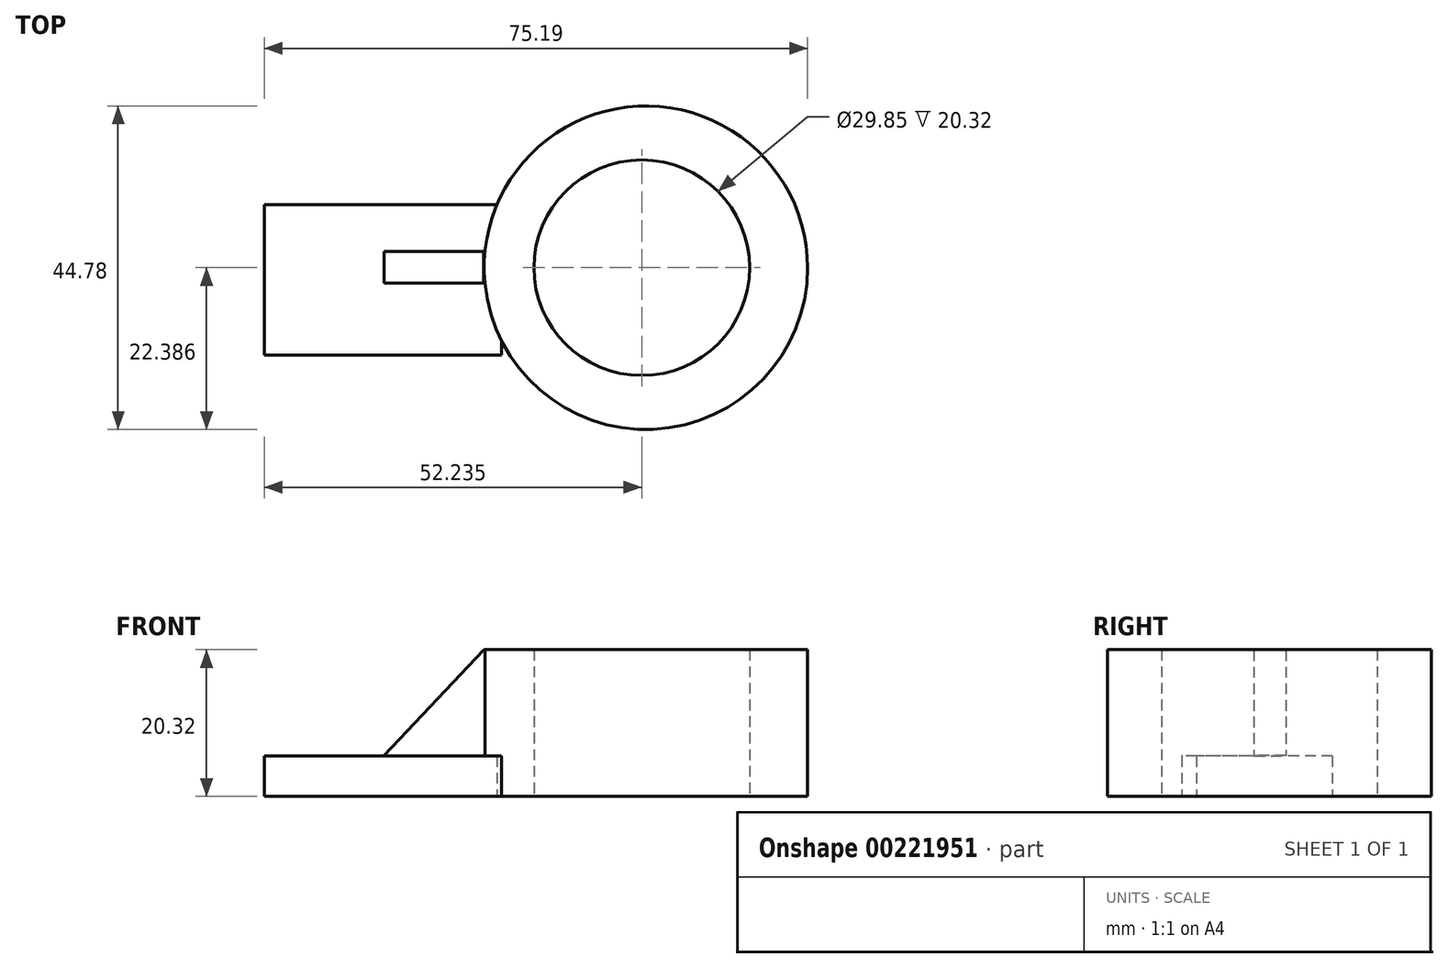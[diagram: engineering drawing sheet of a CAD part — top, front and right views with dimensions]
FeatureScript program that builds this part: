
annotation { "Feature Type Name" : "Feature", "Feature Type Description" : "" }
export const myFeature = defineFeature(function(context is Context, id is Id, definition is map)
    precondition{}
    {
        {
            var Q0;
            Q0=qCreatedBy(makeId("Top.planeOp"),FACE);
            var sketch = newSketch(context, id + "F0", { "sketchPlane" : qUnion([Q0])});
            skCircle(sketch, "E0", {"center": v(36.23, 28.1) * mm, "radius": 22.39 * mm});
            skSolve(sketch);
        }
        {
            var Q0;
            Q0 = qSketchRegion(id + "F0", true);
            extrude(context, id + "F1", {"entities" : qUnion([Q0]), "depth" : 20.32 * mm});
        }
        {
            var Q0;
            Q0=qCreatedBy(makeId("Top.planeOp"),FACE);
            var sketch = newSketch(context, id + "F2", { "sketchPlane" : qUnion([Q0])});
            skCircle(sketch, "E1", {"center": v(35.66, 28.1) * mm, "radius": 14.93 * mm});
            skSolve(sketch);
        }
        {
            var Q0;
            Q0 = qSketchRegion(id + "F2", true);
            extrude(context, id + "F3", {"entities" : qUnion([Q0]), "operationType" : NewBodyOperationType.REMOVE, "endBound" : BoundingType.THROUGH_ALL, "depth" : 43.94 * mm});
        }
        {
            var Q0;
            Q0=qCreatedBy(makeId("Top.planeOp"),FACE);
            var sketch = newSketch(context, id + "F4", { "sketchPlane" : qUnion([Q0])});
            skLineSegment(sketch, "E2.bottom", {"start": v(-16.58, 36.83) * mm, "end": v(16.23, 36.83) * mm});
            skLineSegment(sketch, "E2.top", {"start": v(-16.58, 15.99) * mm, "end": v(16.23, 15.99) * mm});
            skLineSegment(sketch, "E2.left", {"start": v(-16.58, 36.83) * mm, "end": v(-16.58, 15.99) * mm});
            skLineSegment(sketch, "E2.right", {"start": v(16.23, 36.83) * mm, "end": v(16.23, 15.99) * mm});
            skPoint(sketch, "E2.middle", {"position": v(-0.18, 26.41) * mm});
            skSolve(sketch);
        }
        {
            var Q0;
            Q0=makeQuery(id+"F4.imprint","IMPRINT",FACE,{"disambiguationData":[TD([[makeQuery(id+"F4.imprint","IMPRINT",EDGE,{"derivedFrom":sQuery(id+"F4.wireOp",EDGE,"E2.bottom")}),-1.0]])]});
            extrude(context, id + "F5", {"entities" : qUnion([Q0]), "operationType" : NewBodyOperationType.ADD, "depth" : 5.6 * mm});
        }
        {
            var Q0;
            Q0=qCreatedBy(makeId("Right.planeOp"),FACE);
            var sketch = newSketch(context, id + "F6", { "sketchPlane" : qUnion([Q0])});
            skLineSegment(sketch, "E3.bottom", {"start": v(25.97, 5.5) * mm, "end": v(30.38, 5.5) * mm});
            skLineSegment(sketch, "E3.top", {"start": v(25.97, 20.25) * mm, "end": v(30.38, 20.25) * mm});
            skLineSegment(sketch, "E3.left", {"start": v(25.97, 5.5) * mm, "end": v(25.97, 20.25) * mm});
            skLineSegment(sketch, "E3.right", {"start": v(30.38, 5.5) * mm, "end": v(30.38, 20.25) * mm});
            skPoint(sketch, "E3.middle", {"position": v(28.17, 12.88) * mm});
            skSolve(sketch);
        }
        {
            var Q0;
            Q0 = qSketchRegion(id + "F6", true);
            extrude(context, id + "F7", {"entities" : qUnion([Q0]), "operationType" : NewBodyOperationType.ADD, "depth" : 16.76 * mm});
        }
        {
            var Q0;
            Q0=qCreatedBy(makeId("Front.planeOp"),FACE);
            var sketch = newSketch(context, id + "F8", { "sketchPlane" : qUnion([Q0])});
            skLineSegment(sketch, "E4", {"start": v(13.85, 20.34) * mm, "end": v(0, 5.68) * mm});
            skLineSegment(sketch, "E5", {"start": v(0, 5.68) * mm, "end": v(0, 20.85) * mm});
            skLineSegment(sketch, "E6", {"start": v(0, 20.85) * mm, "end": v(13.85, 20.34) * mm});
            skSolve(sketch);
        }
        {
            var Q0;
            Q0 = qSketchRegion(id + "F8", true);
            extrude(context, id + "F9", {"entities" : qUnion([Q0]), "operationType" : NewBodyOperationType.REMOVE, "endBound" : BoundingType.THROUGH_ALL, "oppositeDirection" : true, "depth" : 25.4 * mm});
        }
    });
